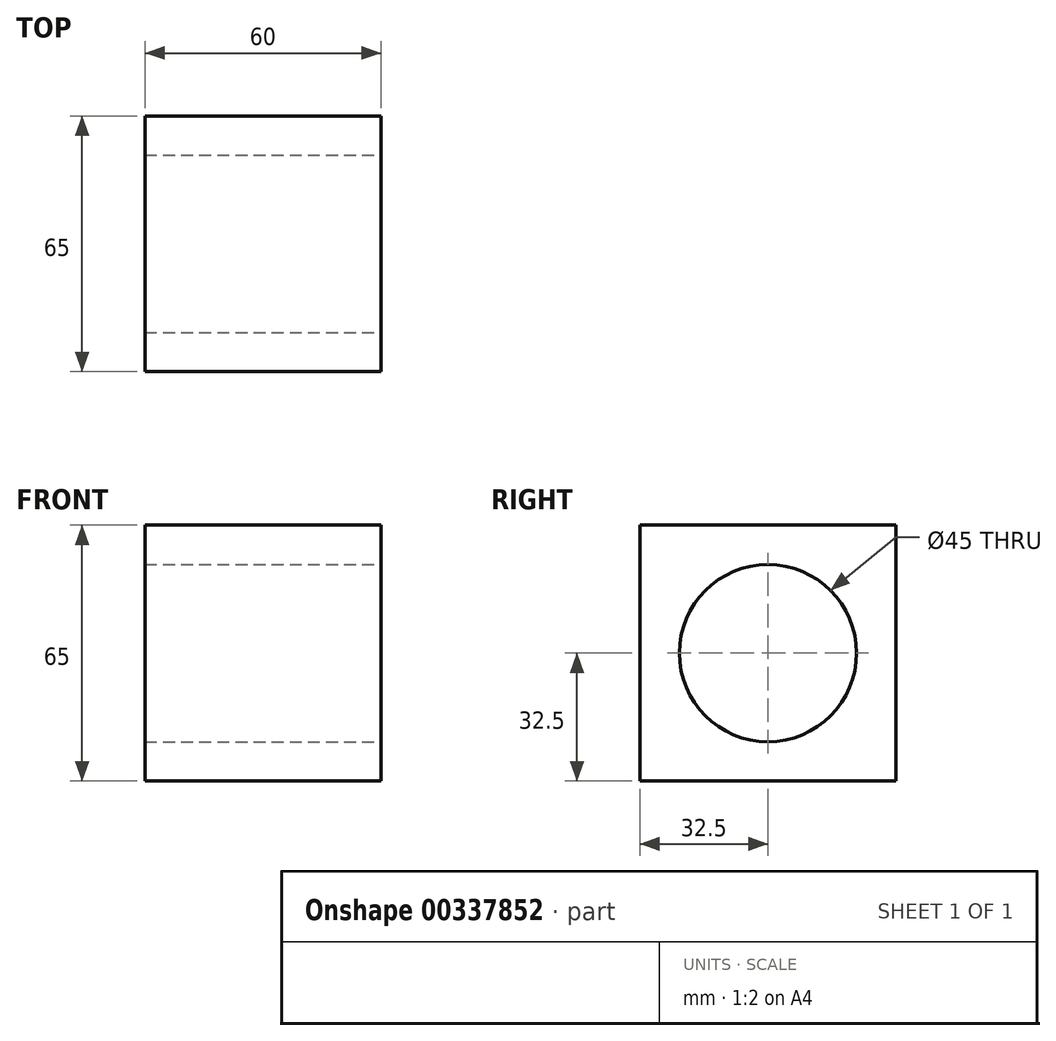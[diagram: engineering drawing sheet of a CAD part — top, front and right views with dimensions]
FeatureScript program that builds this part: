
annotation { "Feature Type Name" : "Feature", "Feature Type Description" : "" }
export const myFeature = defineFeature(function(context is Context, id is Id, definition is map)
    precondition{}
    {
        {
            var Q0;
            Q0=qCreatedBy(makeId("Right.planeOp"),FACE);
            cPlane(context, id + "F0", {"entities" : qUnion([Q0]), "cplaneType" : CPlaneType.OFFSET, "offset" : 100 * mm, "oppositeDirection" : true, "width" : 150 * mm, "height" : 150 * mm});
        }
        {
            var Q0;
            Q0=qCreatedBy(id+"F0.planeOp",FACE);
            var sketch = newSketch(context, id + "F1", { "sketchPlane" : qUnion([Q0])});
            skCircle(sketch, "E0", {"center": v(0, 0) * mm, "radius": 22.5 * mm});
            skLineSegment(sketch, "E1.bottom", {"start": v(32.5, 32.5) * mm, "end": v(-32.5, 32.5) * mm});
            skLineSegment(sketch, "E1.top", {"start": v(32.5, -32.5) * mm, "end": v(-32.5, -32.5) * mm});
            skLineSegment(sketch, "E1.left", {"start": v(32.5, 32.5) * mm, "end": v(32.5, -32.5) * mm});
            skLineSegment(sketch, "E1.right", {"start": v(-32.5, 32.5) * mm, "end": v(-32.5, -32.5) * mm});
            skLineSegment(sketch, "E2", {"start": v(0, 22.5) * mm, "end": v(0, -22.5) * mm, "construction": true});
            skPoint(sketch, "E2.startSnap0", {"position": v(0, 32.5) * mm});
            skLineSegment(sketch, "E3", {"start": v(22.5, 0) * mm, "end": v(-22.5, 0) * mm, "construction": true});
            skSolve(sketch);
        }
        {
            var Q0;
            Q0=makeQuery(id+"F1.imprint","IMPRINT",FACE,{"disambiguationData":[TD([[makeQuery(id+"F1.imprint","IMPRINT",EDGE,{"derivedFrom":sQuery(id+"F1.wireOp",EDGE,"E0")}),-1.0]])]});
            extrude(context, id + "F2", {"entities" : qUnion([Q0]), "oppositeDirection" : true, "depth" : 60 * mm});
        }
    });
